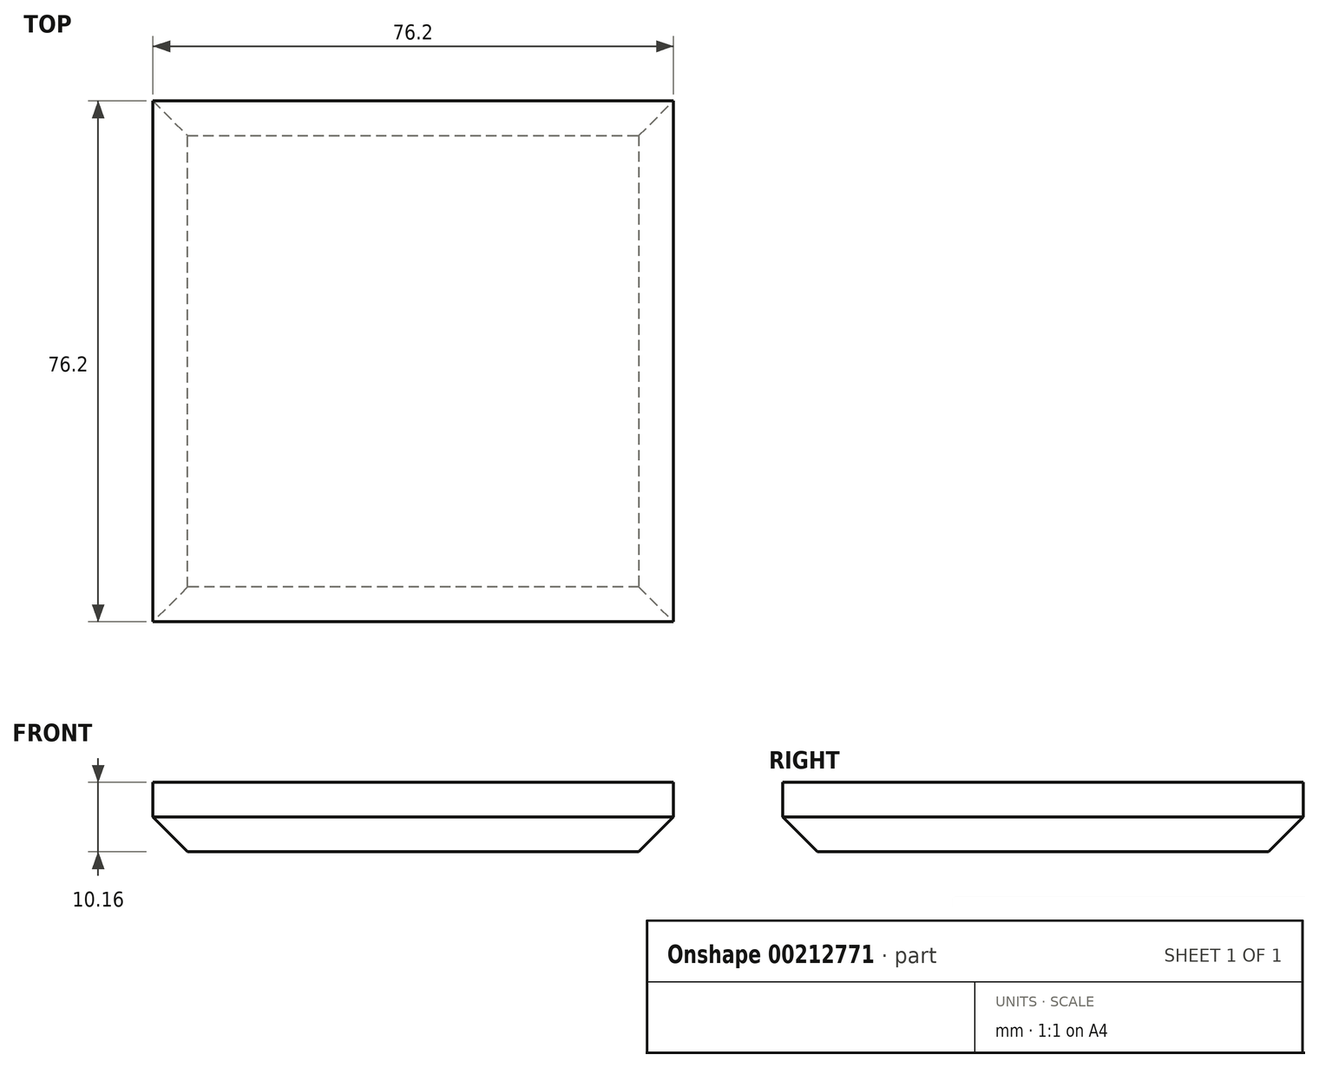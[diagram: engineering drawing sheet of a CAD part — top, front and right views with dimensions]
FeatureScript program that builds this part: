
annotation { "Feature Type Name" : "Feature", "Feature Type Description" : "" }
export const myFeature = defineFeature(function(context is Context, id is Id, definition is map)
    precondition{}
    {
        {
            var Q0;
            Q0=qCreatedBy(makeId("Top.planeOp"),FACE);
            var sketch = newSketch(context, id + "F0", { "sketchPlane" : qUnion([Q0])});
            skLineSegment(sketch, "E0.bottom", {"start": v(-38.1, 38.1) * mm, "end": v(38.1, 38.1) * mm});
            skLineSegment(sketch, "E0.top", {"start": v(-38.1, -38.1) * mm, "end": v(38.1, -38.1) * mm});
            skLineSegment(sketch, "E0.left", {"start": v(-38.1, 38.1) * mm, "end": v(-38.1, -38.1) * mm});
            skLineSegment(sketch, "E0.right", {"start": v(38.1, 38.1) * mm, "end": v(38.1, -38.1) * mm});
            skPoint(sketch, "E0.middle", {"position": v(0, 0) * mm});
            skSolve(sketch);
        }
        {
            var Q0;
            Q0=makeQuery(id+"F0.imprint","IMPRINT",FACE,{"disambiguationData":[TD([[makeQuery(id+"F0.imprint","IMPRINT",EDGE,{"derivedFrom":sQuery(id+"F0.wireOp",EDGE,"E0.bottom")}),-1.0]])]});
            extrude(context, id + "F1", {"entities" : qUnion([Q0]), "depth" : 10.16 * mm});
        }
        {
            var Q0;
            Q0=makeQuery(id+"F1.opExtrude","CAP_EDGE",EDGE,{"disambiguationData":[OSD([sQuery(id+"F0.wireOp",EDGE,"E0.bottom")])],"isStart":true});
            var Q1;
            Q1=makeQuery(id+"F1.opExtrude","CAP_EDGE",EDGE,{"disambiguationData":[OSD([sQuery(id+"F0.wireOp",EDGE,"E0.right")])],"isStart":true});
            var Q2;
            Q2=makeQuery(id+"F1.opExtrude","CAP_EDGE",EDGE,{"disambiguationData":[OSD([sQuery(id+"F0.wireOp",EDGE,"E0.top")])],"isStart":true});
            var Q3;
            Q3=makeQuery(id+"F1.opExtrude","CAP_EDGE",EDGE,{"disambiguationData":[OSD([sQuery(id+"F0.wireOp",EDGE,"E0.left")])],"isStart":true});
            chamfer(context, id + "F2", {"entities" : qUnion([Q0, Q1, Q2, Q3]), "width" : 5.08 * mm, "tangentPropagation" : true});
        }
        {
            var Q0;
            Q0=qCreatedBy(makeId("Front.planeOp"),FACE);
            var sketch = newSketch(context, id + "F3", { "sketchPlane" : qUnion([Q0])});
            skArc(sketch, "E1", {"start": v(-25.49, 0) * mm, "mid": v(0, -25.49) * mm, "end": v(25.49, 0) * mm});
            skSolve(sketch);
        }
        {
            var Q0;
            Q0=sQuery(id+"F3.wireOp",EDGE,"E1");
            extrude(context, id + "F4", {"bodyType" : ToolBodyType.SURFACE, "surfaceEntities" : qUnion([Q0]), "depth" : 12.7 * mm});
        }
        {
            var Q0;
            Q0=sQuery(id+"F3.wireOp",EDGE,"E1");
            extrude(context, id + "F5", {"bodyType" : ToolBodyType.SURFACE, "surfaceEntities" : qUnion([Q0]), "oppositeDirection" : true, "depth" : 12.7 * mm});
        }
    });
